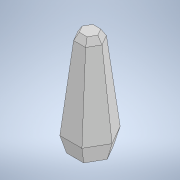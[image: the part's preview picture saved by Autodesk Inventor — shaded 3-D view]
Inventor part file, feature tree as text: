
AUTODESK INVENTOR PART (.ipt)
format: ipt  version: 2022 (Build 260153000, 153)  size: 136,192 bytes
history: native  units: in
note: dims shown in document units (in); Inventor stores cm internally (conversion verified against a paired STEP export)
features: sketch x4, sweep x1, revolve x1, extrude x1
ambient origin geometry x8: Origin, YZ Plane, XZ Plane, XY Plane, X Axis, Y Axis, Z Axis, Center Point
bodies: Solid1 (feature_tree)
feature tree (7):
  sweep  "Sweep1"
  revolve  "Revolution1"  [1 undecoded]
  extrude  "Extrusion1"  Depth=0.125in
  sketch  "Sketch1"  dims[d0=0.75in d1=0.75in]
  sketch  "Sketch3"  dims[d3=0.0in d4=0.0in d6=4.5in]
  sketch  "Sketch4"  dims[d11=90.0deg d12=0.125in]
  sketch  "Sketch5"  dims[d13=0.932in d14=0.0in]
note: 1 required parameter value undecoded (feature->parameter linkage not recoverable at this tier; creation-order binding heuristic only, values carry confidence <= 0.55)
